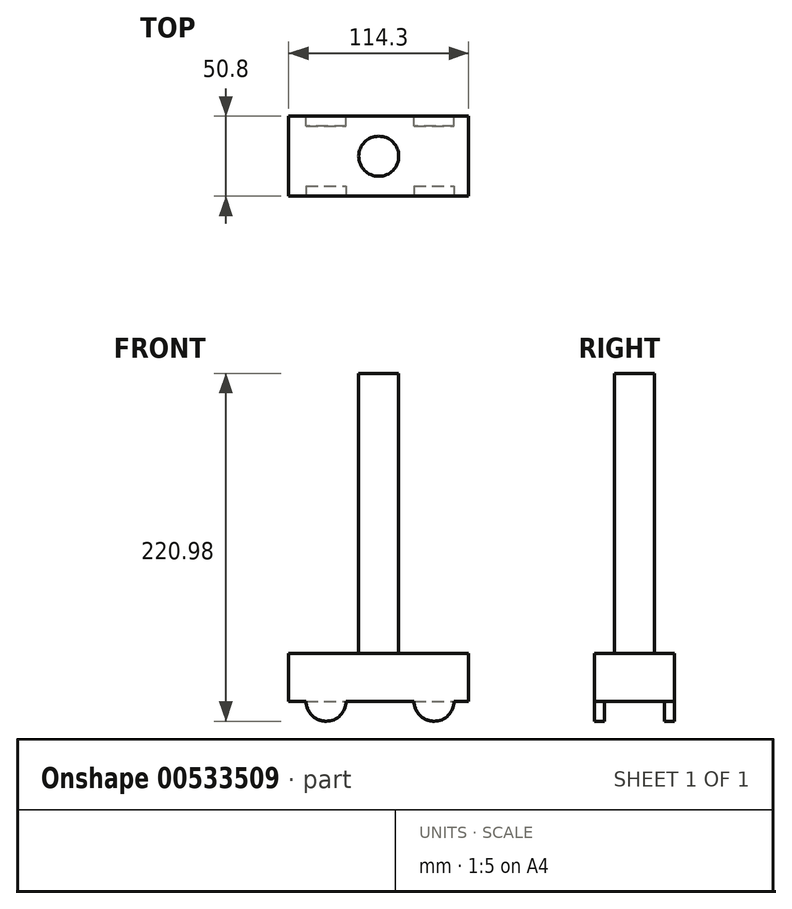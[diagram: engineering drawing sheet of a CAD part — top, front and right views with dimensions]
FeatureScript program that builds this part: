
annotation { "Feature Type Name" : "Feature", "Feature Type Description" : "" }
export const myFeature = defineFeature(function(context is Context, id is Id, definition is map)
    precondition{}
    {
        {
            var Q0;
            Q0=qCreatedBy(makeId("Top.planeOp"),FACE);
            var sketch = newSketch(context, id + "F0", { "sketchPlane" : qUnion([Q0])});
            skLineSegment(sketch, "E0.bottom", {"start": v(-57.15, 25.4) * mm, "end": v(57.15, 25.4) * mm});
            skLineSegment(sketch, "E0.top", {"start": v(-57.15, -25.4) * mm, "end": v(57.15, -25.4) * mm});
            skLineSegment(sketch, "E0.left", {"start": v(-57.15, 25.4) * mm, "end": v(-57.15, -25.4) * mm});
            skLineSegment(sketch, "E0.right", {"start": v(57.15, 25.4) * mm, "end": v(57.15, -25.4) * mm});
            skPoint(sketch, "E0.middle", {"position": v(0, 0) * mm});
            skSolve(sketch);
        }
        {
            var Q0;
            Q0=makeQuery(id+"F0.imprint","IMPRINT",FACE,{"disambiguationData":[TD([[makeQuery(id+"F0.imprint","IMPRINT",EDGE,{"derivedFrom":sQuery(id+"F0.wireOp",EDGE,"E0.bottom")}),-1.0]])]});
            extrude(context, id + "F1", {"entities" : qUnion([Q0]), "depth" : 30.48 * mm, "offsetDistance" : 25.4 * mm});
        }
        {
            var Q0;
            Q0=makeQuery(id+"F1.opExtrude","CAP_FACE",FACE,{"disambiguationData":[OSD([sQuery(id+"F0.wireOp",EDGE,"E0.bottom"),sQuery(id+"F0.wireOp",EDGE,"E0.top"),sQuery(id+"F0.wireOp",EDGE,"E0.left"),sQuery(id+"F0.wireOp",EDGE,"E0.right")])],"isStart":false});
            var sketch = newSketch(context, id + "F2", { "sketchPlane" : qUnion([Q0])});
            skCircle(sketch, "E1", {"center": v(0, 0) * mm, "radius": 12.7 * mm});
            skSolve(sketch);
        }
        {
            var Q0;
            Q0=makeQuery(id+"F2.imprint","IMPRINT",FACE,{"disambiguationData":[TD([[makeQuery(id+"F2.imprint","IMPRINT",EDGE,{"derivedFrom":sQuery(id+"F2.wireOp",EDGE,"E1")}),1.0]])]});
            extrude(context, id + "F3", {"entities" : qUnion([Q0]), "operationType" : NewBodyOperationType.ADD, "depth" : 177.8 * mm, "offsetDistance" : 25.4 * mm});
        }
        {
            var Q0;
            Q0=makeQuery(id+"F1.opExtrude","SWEPT_FACE",FACE,{"disambiguationData":[OSD([sQuery(id+"F0.wireOp",EDGE,"E0.bottom")])]});
            var sketch = newSketch(context, id + "F4", { "sketchPlane" : qUnion([Q0])});
            skCircle(sketch, "E2", {"center": v(-35.14, 0) * mm, "radius": 12.7 * mm});
            skCircle(sketch, "E3", {"center": v(33.44, 0) * mm, "radius": 12.7 * mm});
            skSolve(sketch);
        }
        {
            var Q0;
            {var subQ0=sQuery(id+"F4.wireOp",EDGE,"E2");var subQ1=makeQuery(id+"F1.opExtrude","CAP_EDGE",EDGE,{"disambiguationData":[OSD([sQuery(id+"F0.wireOp",EDGE,"E0.bottom")])],"isStart":true});var subQ2=makeQuery(id+"F4.imprint","INTERSECT",VERTEX,{"disambiguationData":[OD(0.0)],"derivedFrom":[subQ1,subQ0]});Q0=makeQuery(id+"F4.imprint","IMPRINT",FACE,{"disambiguationData":[TD([[makeQuery(id+"F4.imprint","IMPRINT",EDGE,{"disambiguationData":[TD([[subQ2,-1.0]])],"derivedFrom":subQ0}),1.0]])]});}
            var Q1;
            {var subQ0=sQuery(id+"F4.wireOp",EDGE,"E3");var subQ1=makeQuery(id+"F1.opExtrude","CAP_EDGE",EDGE,{"disambiguationData":[OSD([sQuery(id+"F0.wireOp",EDGE,"E0.bottom")])],"isStart":true});var subQ2=makeQuery(id+"F4.imprint","INTERSECT",VERTEX,{"disambiguationData":[OD(0.0)],"derivedFrom":[subQ1,subQ0]});Q1=makeQuery(id+"F4.imprint","IMPRINT",FACE,{"disambiguationData":[TD([[makeQuery(id+"F4.imprint","IMPRINT",EDGE,{"disambiguationData":[TD([[subQ2,1.0]])],"derivedFrom":subQ0}),1.0]])]});}
            extrude(context, id + "F5", {"entities" : qUnion([Q0, Q1]), "operationType" : NewBodyOperationType.ADD, "oppositeDirection" : true, "depth" : 6.35 * mm, "offsetDistance" : 25.4 * mm});
        }
        {
            var Q0;
            Q0=makeQuery(id+"F1.opExtrude","SWEPT_FACE",FACE,{"disambiguationData":[OSD([sQuery(id+"F0.wireOp",EDGE,"E0.top")])]});
            var sketch = newSketch(context, id + "F6", { "sketchPlane" : qUnion([Q0])});
            skCircle(sketch, "E4", {"center": v(-33.43, 0) * mm, "radius": 12.7 * mm});
            skCircle(sketch, "E5", {"center": v(35.15, 0) * mm, "radius": 12.7 * mm});
            skSolve(sketch);
        }
        {
            var Q0;
            {var subQ0=sQuery(id+"F6.wireOp",EDGE,"E4");var subQ1=makeQuery(id+"F1.opExtrude","CAP_EDGE",EDGE,{"disambiguationData":[OSD([sQuery(id+"F0.wireOp",EDGE,"E0.top")])],"isStart":true});var subQ2=makeQuery(id+"F6.imprint","INTERSECT",VERTEX,{"disambiguationData":[OD(0.0)],"derivedFrom":[subQ1,subQ0]});Q0=makeQuery(id+"F6.imprint","IMPRINT",FACE,{"disambiguationData":[TD([[makeQuery(id+"F6.imprint","IMPRINT",EDGE,{"disambiguationData":[TD([[subQ2,-1.0]])],"derivedFrom":subQ0}),1.0]])]});}
            var Q1;
            {var subQ0=sQuery(id+"F6.wireOp",EDGE,"E5");var subQ1=makeQuery(id+"F1.opExtrude","CAP_EDGE",EDGE,{"disambiguationData":[OSD([sQuery(id+"F0.wireOp",EDGE,"E0.top")])],"isStart":true});var subQ2=makeQuery(id+"F6.imprint","INTERSECT",VERTEX,{"disambiguationData":[OD(0.0)],"derivedFrom":[subQ1,subQ0]});Q1=makeQuery(id+"F6.imprint","IMPRINT",FACE,{"disambiguationData":[TD([[makeQuery(id+"F6.imprint","IMPRINT",EDGE,{"disambiguationData":[TD([[subQ2,1.0]])],"derivedFrom":subQ0}),1.0]])]});}
            extrude(context, id + "F7", {"entities" : qUnion([Q0, Q1]), "operationType" : NewBodyOperationType.ADD, "oppositeDirection" : true, "depth" : 6.35 * mm, "offsetDistance" : 25.4 * mm});
        }
    });
